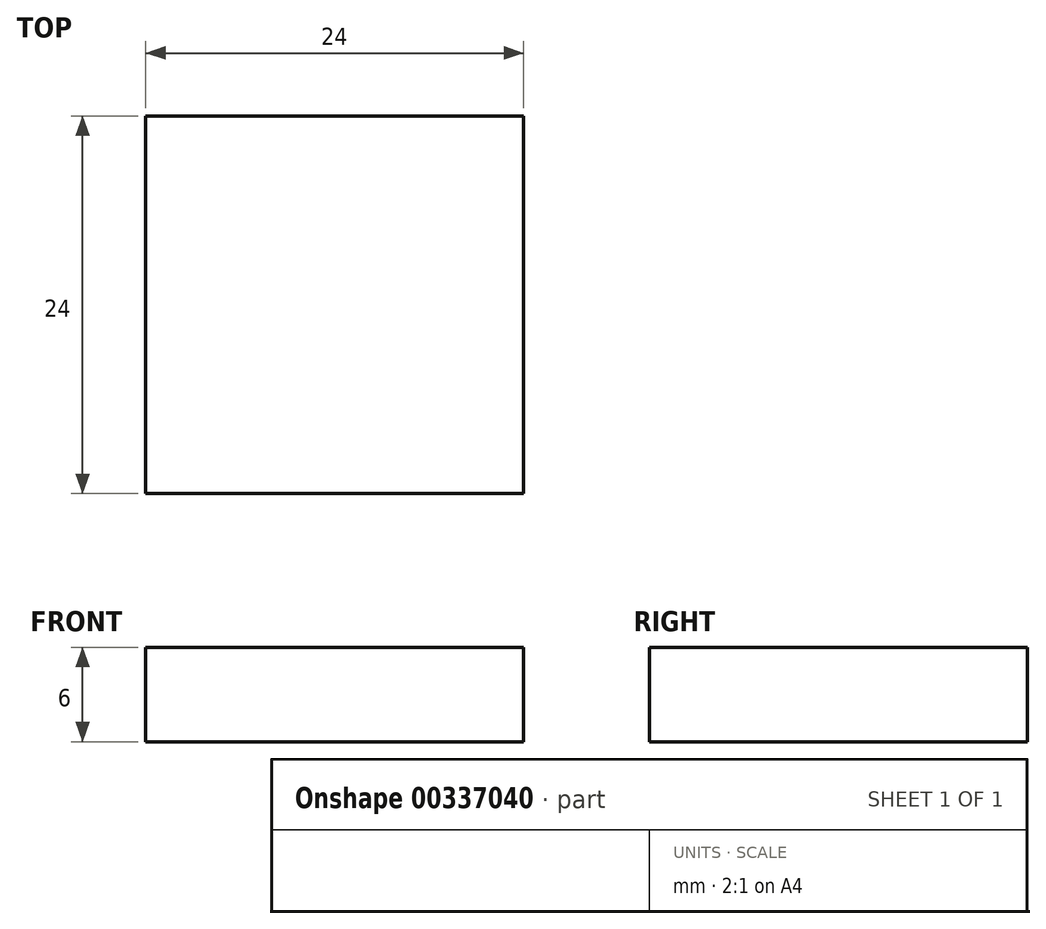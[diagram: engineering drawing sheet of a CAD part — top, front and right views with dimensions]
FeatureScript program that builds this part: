
annotation { "Feature Type Name" : "Feature", "Feature Type Description" : "" }
export const myFeature = defineFeature(function(context is Context, id is Id, definition is map)
    precondition{}
    {
        {
            var Q0;
            Q0=qCreatedBy(makeId("Top.planeOp"),FACE);
            var sketch = newSketch(context, id + "F0", { "sketchPlane" : qUnion([Q0])});
            skLineSegment(sketch, "E0", {"start": v(-12, 12) * mm, "end": v(-12, -12) * mm});
            skLineSegment(sketch, "E1", {"start": v(-12, -12) * mm, "end": v(12, -12) * mm});
            skLineSegment(sketch, "E2", {"start": v(12, -12) * mm, "end": v(12, 12) * mm});
            skLineSegment(sketch, "E3", {"start": v(12, 12) * mm, "end": v(-12, 12) * mm});
            skSolve(sketch);
        }
        {
            var Q0;
            Q0=makeQuery(id+"F0.imprint","IMPRINT",FACE,{"disambiguationData":[TD([[makeQuery(id+"F0.imprint","IMPRINT",EDGE,{"derivedFrom":sQuery(id+"F0.wireOp",EDGE,"E0")}),1.0]])]});
            extrude(context, id + "F1", {"entities" : qUnion([Q0]), "depth" : 6 * mm});
        }
        {
            var Q0;
            Q0=qCreatedBy(makeId("Front.planeOp"),FACE);
            cPlane(context, id + "F2", {"entities" : qUnion([Q0]), "cplaneType" : CPlaneType.OFFSET, "offset" : 6 * mm, "width" : 150 * mm, "height" : 150 * mm});
        }
        {
            var Q0;
            Q0=qCreatedBy(makeId("Front.planeOp"),FACE);
            cPlane(context, id + "F3", {"entities" : qUnion([Q0]), "cplaneType" : CPlaneType.OFFSET, "offset" : 6 * mm, "oppositeDirection" : true, "width" : 150 * mm, "height" : 150 * mm});
        }
    });
